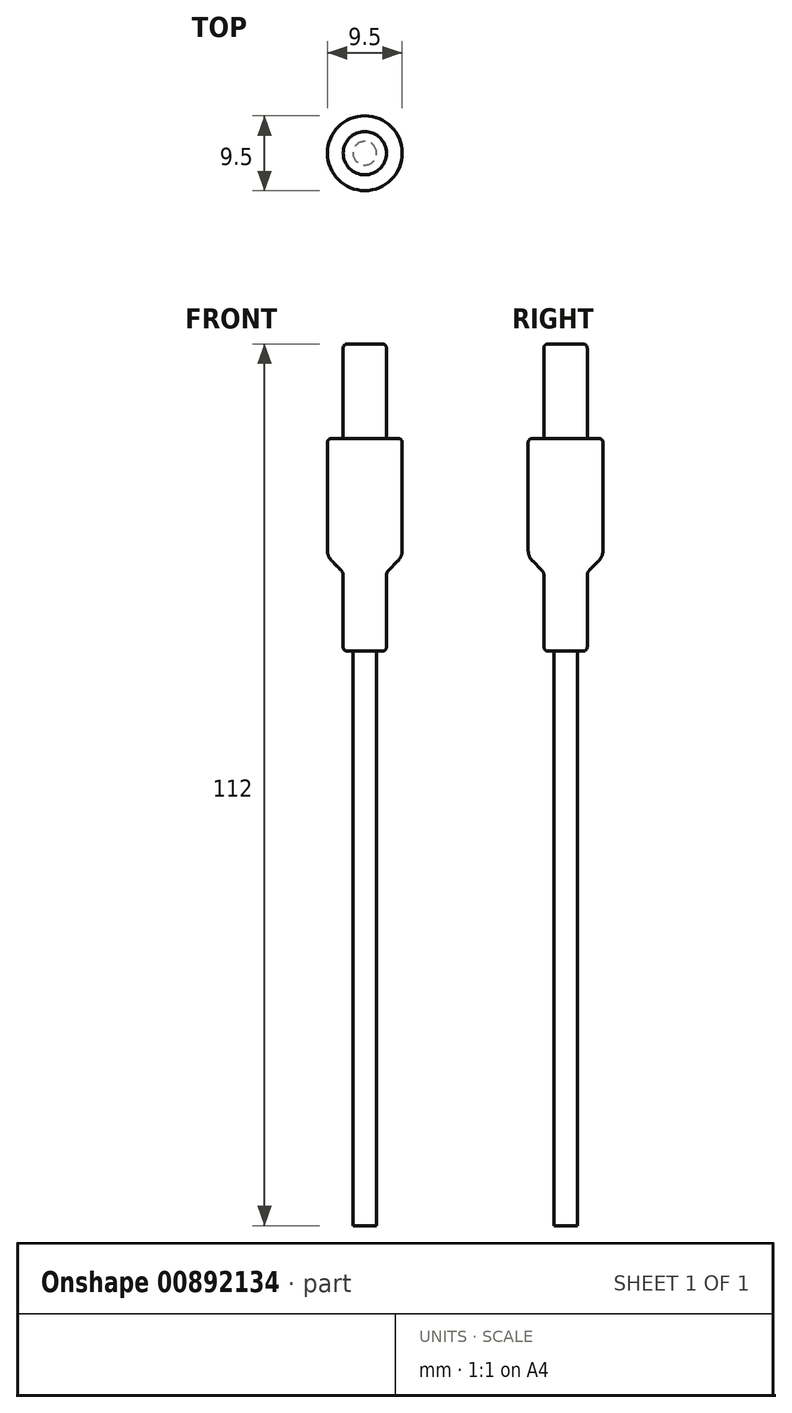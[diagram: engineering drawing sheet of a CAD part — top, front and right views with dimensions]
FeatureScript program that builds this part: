
annotation { "Feature Type Name" : "Feature", "Feature Type Description" : "" }
export const myFeature = defineFeature(function(context is Context, id is Id, definition is map)
    precondition{}
    {
        {
            var Q0;
            Q0=qCreatedBy(makeId("Top.planeOp"),FACE);
            var sketch = newSketch(context, id + "F0", { "sketchPlane" : qUnion([Q0])});
            skCircle(sketch, "E0", {"center": v(0, 0) * mm, "radius": 2.75 * mm});
            skCircle(sketch, "E1", {"center": v(0, 0) * mm, "radius": 4.75 * mm});
            skCircle(sketch, "E2", {"center": v(0, 0) * mm, "radius": 1.5 * mm});
            skSolve(sketch);
        }
        {
            var Q0;
            Q0=makeQuery(id+"F0.imprint","IMPRINT",FACE,{"disambiguationData":[TD([[makeQuery(id+"F0.imprint","IMPRINT",EDGE,{"derivedFrom":sQuery(id+"F0.wireOp",EDGE,"E0")}),1.0]])]});
            var Q1;
            Q1=makeQuery(id+"F0.imprint","IMPRINT",FACE,{"disambiguationData":[TD([[makeQuery(id+"F0.imprint","IMPRINT",EDGE,{"derivedFrom":sQuery(id+"F0.wireOp",EDGE,"E2")}),1.0]])]});
            extrude(context, id + "F1", {"entities" : qUnion([Q0, Q1]), "depth" : 12 * mm, "offsetDistance" : 25 * mm});
        }
        {
            var Q0;
            Q0=makeQuery(id+"F0.imprint","IMPRINT",FACE,{"disambiguationData":[TD([[makeQuery(id+"F0.imprint","IMPRINT",EDGE,{"derivedFrom":sQuery(id+"F0.wireOp",EDGE,"E2")}),1.0]])]});
            extrude(context, id + "F2", {"entities" : qUnion([Q0]), "operationType" : NewBodyOperationType.ADD, "oppositeDirection" : true, "depth" : 100 * mm, "offsetDistance" : 25 * mm});
        }
        {
            var Q0;
            Q0=makeQuery(id+"F0.imprint","IMPRINT",FACE,{"disambiguationData":[TD([[makeQuery(id+"F0.imprint","IMPRINT",EDGE,{"derivedFrom":sQuery(id+"F0.wireOp",EDGE,"E0")}),1.0]])]});
            var Q1;
            Q1=makeQuery(id+"F0.imprint","IMPRINT",FACE,{"disambiguationData":[TD([[makeQuery(id+"F0.imprint","IMPRINT",EDGE,{"derivedFrom":sQuery(id+"F0.wireOp",EDGE,"E2")}),1.0]])]});
            extrude(context, id + "F3", {"entities" : qUnion([Q0, Q1]), "operationType" : NewBodyOperationType.ADD, "oppositeDirection" : true, "depth" : 27 * mm, "offsetDistance" : 25 * mm});
        }
        {
            var Q0;
            Q0=makeQuery(id+"F0.imprint","IMPRINT",FACE,{"disambiguationData":[TD([[makeQuery(id+"F0.imprint","IMPRINT",EDGE,{"derivedFrom":sQuery(id+"F0.wireOp",EDGE,"E2")}),1.0]])]});
            var Q1;
            Q1=makeQuery(id+"F0.imprint","IMPRINT",FACE,{"disambiguationData":[TD([[makeQuery(id+"F0.imprint","IMPRINT",EDGE,{"derivedFrom":sQuery(id+"F0.wireOp",EDGE,"E0")}),1.0]])]});
            var Q2;
            Q2=makeQuery(id+"F0.imprint","IMPRINT",FACE,{"disambiguationData":[TD([[makeQuery(id+"F0.imprint","IMPRINT",EDGE,{"derivedFrom":sQuery(id+"F0.wireOp",EDGE,"E0")}),-1.0]])]});
            extrude(context, id + "F4", {"entities" : qUnion([Q0, Q1, Q2]), "operationType" : NewBodyOperationType.ADD, "oppositeDirection" : true, "depth" : 17 * mm, "offsetDistance" : 25 * mm});
        }
        {
            var Q0;
            Q0=makeQuery(id+"F4.opExtrude","CAP_EDGE",EDGE,{"disambiguationData":[OSD([sQuery(id+"F0.wireOp",EDGE,"E1")])],"isStart":false});
            chamfer(context, id + "F5", {"entities" : qUnion([Q0]), "width" : 2 * mm, "tangentPropagation" : true});
        }
        {
            var Q0;
            {var subQ0=sQuery(id+"F0.wireOp",EDGE,"E1");Q0=makeQuery(id+"F5.opChamfer","BLEND_EDGE",EDGE,{"blendedFrom":[makeQuery(id+"F4.opExtrude","CAP_EDGE",EDGE,{"disambiguationData":[OSD([subQ0])],"isStart":false}),makeQuery(id+"F4.opExtrude","SWEPT_FACE",FACE,{"disambiguationData":[OSD([subQ0])]})],"blendedInto":[makeQuery(id+"F4.opExtrude","SWEPT_FACE",FACE,{"disambiguationData":[OSD([subQ0])]})]});}
            fillet(context, id + "F6", {"entities" : qUnion([Q0]), "radius" : 2 * mm, "tangentPropagation" : true, "allowEdgeOverflow" : false});
        }
        {
            var Q0;
            {var subQ0=sQuery(id+"F0.wireOp",EDGE,"E0");var subQ1=sQuery(id+"F0.wireOp",EDGE,"E1");Q0=makeQuery(id+"F5.opChamfer","BLEND_EDGE",EDGE,{"blendedFrom":[makeQuery(id+"F4.opExtrude","CAP_EDGE",EDGE,{"disambiguationData":[OSD([subQ1])],"isStart":false}),makeQuery(id+"F4.boolean.opBoolean","SPLIT",FACE,{"disambiguationData":[TD([makeQuery(id+"F3.opExtrude","CAP_FACE",FACE,{"disambiguationData":[OSD([subQ0])],"isStart":false})])],"derivedFrom":makeQuery(id+"F3.boolean.opBoolean","MERGE",FACE,{"derivedFrom":[makeQuery(id+"F1.opExtrude","SWEPT_FACE",FACE,{"disambiguationData":[OSD([subQ0])]}),makeQuery(id+"F3.opExtrude","SWEPT_FACE",FACE,{"disambiguationData":[OSD([subQ0])]})]})})],"blendedInto":[makeQuery(id+"F4.boolean.opBoolean","SPLIT",FACE,{"disambiguationData":[TD([makeQuery(id+"F3.opExtrude","CAP_FACE",FACE,{"disambiguationData":[OSD([subQ0])],"isStart":false})])],"derivedFrom":makeQuery(id+"F3.boolean.opBoolean","MERGE",FACE,{"derivedFrom":[makeQuery(id+"F1.opExtrude","SWEPT_FACE",FACE,{"disambiguationData":[OSD([subQ0])]}),makeQuery(id+"F3.opExtrude","SWEPT_FACE",FACE,{"disambiguationData":[OSD([subQ0])]})]})})]});}
            fillet(context, id + "F7", {"entities" : qUnion([Q0]), "radius" : 1 * mm, "tangentPropagation" : true, "allowEdgeOverflow" : false});
        }
        {
            var Q0;
            Q0=makeQuery(id+"F4.opExtrude","CAP_EDGE",EDGE,{"disambiguationData":[OSD([sQuery(id+"F0.wireOp",EDGE,"E1")])],"isStart":true});
            var Q1;
            Q1=makeQuery(id+"F1.opExtrude","CAP_EDGE",EDGE,{"disambiguationData":[OSD([sQuery(id+"F0.wireOp",EDGE,"E0")])],"isStart":false});
            var Q2;
            Q2=makeQuery(id+"F3.opExtrude","CAP_EDGE",EDGE,{"disambiguationData":[OSD([sQuery(id+"F0.wireOp",EDGE,"E0")])],"isStart":false});
            fillet(context, id + "F8", {"entities" : qUnion([Q0, Q1, Q2]), "radius" : 0.5 * mm, "tangentPropagation" : true, "allowEdgeOverflow" : false});
        }
    });
